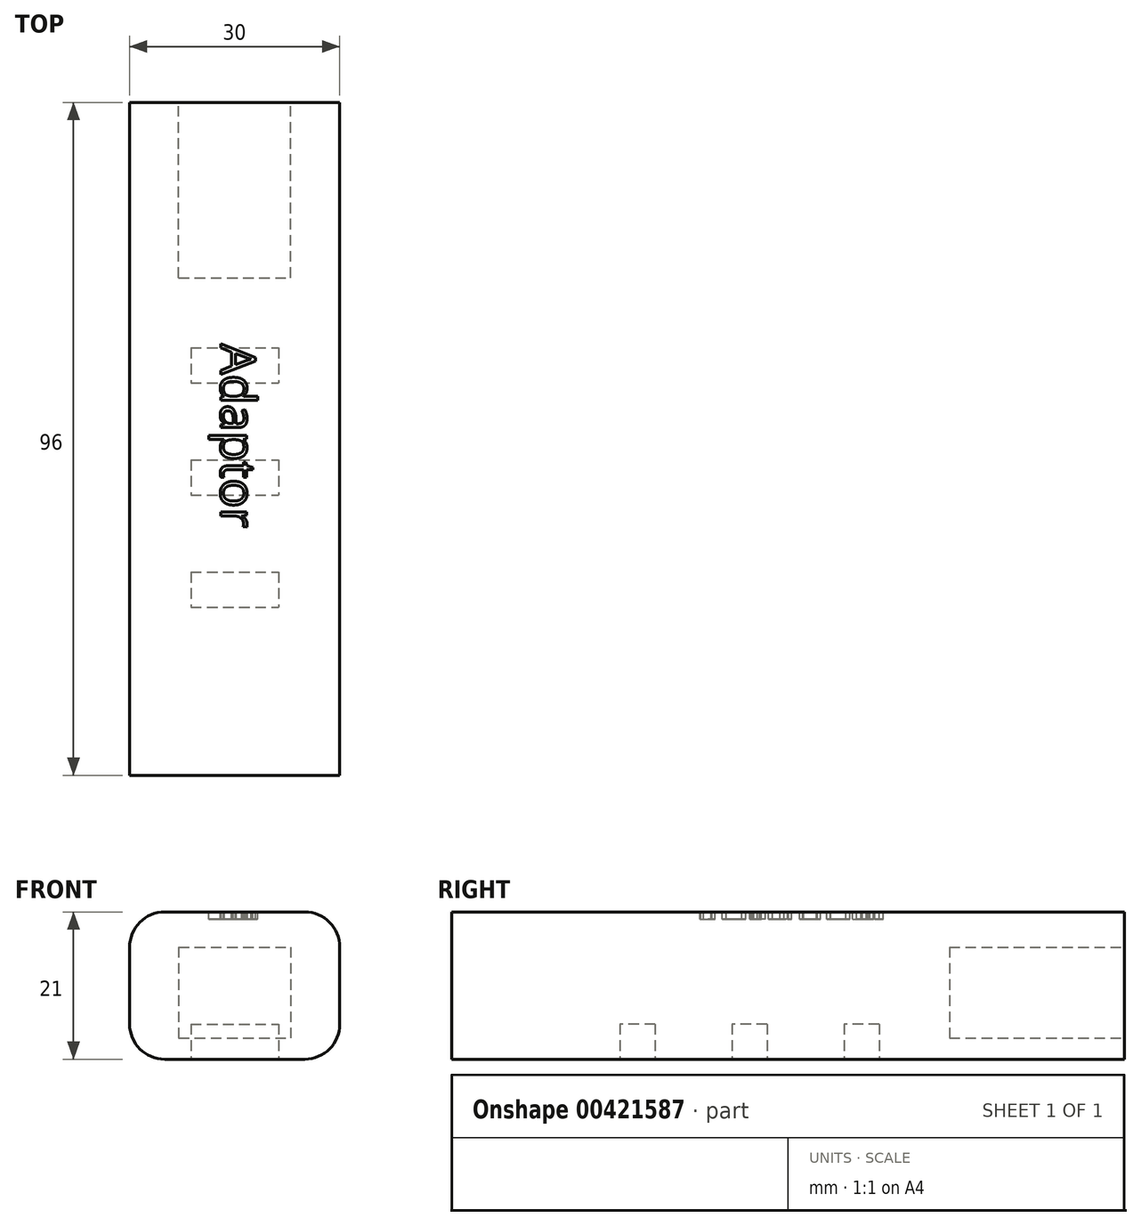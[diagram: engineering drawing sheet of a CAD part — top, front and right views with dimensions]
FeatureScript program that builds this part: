
annotation { "Feature Type Name" : "Feature", "Feature Type Description" : "" }
export const myFeature = defineFeature(function(context is Context, id is Id, definition is map)
    precondition{}
    {
        {
            var Q0;
            Q0=qCreatedBy(makeId("Top.planeOp"),FACE);
            var sketch = newSketch(context, id + "F0", { "sketchPlane" : qUnion([Q0])});
            skLineSegment(sketch, "E0.bottom", {"start": v(15, 48) * mm, "end": v(-15, 48) * mm});
            skLineSegment(sketch, "E0.top", {"start": v(15, -48) * mm, "end": v(-15, -48) * mm});
            skLineSegment(sketch, "E0.left", {"start": v(15, 48) * mm, "end": v(15, -48) * mm});
            skLineSegment(sketch, "E0.right", {"start": v(-15, 48) * mm, "end": v(-15, -48) * mm});
            skPoint(sketch, "E0.middle", {"position": v(0, 0) * mm});
            skSolve(sketch);
        }
        {
            var Q0;
            Q0 = qSketchRegion(id + "F0", true);
            extrude(context, id + "F1", {"entities" : qUnion([Q0]), "depth" : 21 * mm, "offsetDistance" : 25 * mm});
        }
        {
            var Q0;
            Q0=makeQuery(id+"F1.opExtrude","CAP_EDGE",EDGE,{"disambiguationData":[OSD([sQuery(id+"F0.wireOp",EDGE,"E0.left")])],"isStart":false});
            var Q1;
            Q1=makeQuery(id+"F1.opExtrude","CAP_EDGE",EDGE,{"disambiguationData":[OSD([sQuery(id+"F0.wireOp",EDGE,"E0.right")])],"isStart":false});
            var Q2;
            Q2=makeQuery(id+"F1.opExtrude","CAP_EDGE",EDGE,{"disambiguationData":[OSD([sQuery(id+"F0.wireOp",EDGE,"E0.left")])],"isStart":true});
            var Q3;
            Q3=makeQuery(id+"F1.opExtrude","CAP_EDGE",EDGE,{"disambiguationData":[OSD([sQuery(id+"F0.wireOp",EDGE,"E0.right")])],"isStart":true});
            fillet(context, id + "F2", {"entities" : qUnion([Q0, Q1, Q2, Q3]), "radius" : 5 * mm, "tangentPropagation" : true, "allowEdgeOverflow" : false});
        }
        {
            var Q0;
            Q0=makeQuery(id+"F1.opExtrude","SWEPT_FACE",FACE,{"disambiguationData":[OSD([sQuery(id+"F0.wireOp",EDGE,"E0.bottom")])]});
            var sketch = newSketch(context, id + "F3", { "sketchPlane" : qUnion([Q0])});
            skLineSegment(sketch, "E1.bottom", {"start": v(8, 16) * mm, "end": v(-8, 16) * mm});
            skLineSegment(sketch, "E1.top", {"start": v(8, 3) * mm, "end": v(-8, 3) * mm});
            skLineSegment(sketch, "E1.left", {"start": v(8, 16) * mm, "end": v(8, 3) * mm});
            skLineSegment(sketch, "E1.right", {"start": v(-8, 16) * mm, "end": v(-8, 3) * mm});
            skPoint(sketch, "E1.middle", {"position": v(0, 9.5) * mm});
            skSolve(sketch);
        }
        {
            var Q0;
            Q0=makeQuery(id+"F3.imprint","IMPRINT",FACE,{"disambiguationData":[TD([[makeQuery(id+"F3.imprint","IMPRINT",EDGE,{"derivedFrom":sQuery(id+"F3.wireOp",EDGE,"E1.bottom")}),1.0]])]});
            extrude(context, id + "F4", {"entities" : qUnion([Q0]), "operationType" : NewBodyOperationType.REMOVE, "oppositeDirection" : true, "depth" : 25 * mm, "offsetDistance" : 25 * mm});
        }
        {
            var Q0;
            Q0=makeQuery(id+"F1.opExtrude","CAP_FACE",FACE,{"disambiguationData":[OSD([sQuery(id+"F0.wireOp",EDGE,"E0.bottom"),sQuery(id+"F0.wireOp",EDGE,"E0.top"),sQuery(id+"F0.wireOp",EDGE,"E0.left"),sQuery(id+"F0.wireOp",EDGE,"E0.right")])],"isStart":false});
            cPlane(context, id + "F5", {"entities" : qUnion([Q0]), "cplaneType" : CPlaneType.OFFSET, "offset" : 0 * mm, "width" : 150 * mm, "height" : 150 * mm});
        }
        {
            var Q0;
            Q0=qCreatedBy(id+"F5.planeOp",FACE);
            var sketch = newSketch(context, id + "F6", { "sketchPlane" : qUnion([Q0])});
            skText(sketch, "E2", { "text": "Adaptor\n", "fontName": "OpenSans-Regular.ttf"});
            const initialGuessF6  = {"E2": [-0.00201, 0.01358, 0, -1, 0.005]};
            skSetInitialGuess(sketch, initialGuessF6);
            skSolve(sketch);
        }
        {
            var Q0;
            Q0 = qSketchRegion(id + "F6", true);
            extrude(context, id + "F7", {"entities" : qUnion([Q0]), "operationType" : NewBodyOperationType.REMOVE, "oppositeDirection" : true, "depth" : 1 * mm, "offsetDistance" : 25 * mm});
        }
        {
            var Q0;
            Q0=makeQuery(id+"F1.opExtrude","CAP_FACE",FACE,{"disambiguationData":[OSD([sQuery(id+"F0.wireOp",EDGE,"E0.bottom"),sQuery(id+"F0.wireOp",EDGE,"E0.top"),sQuery(id+"F0.wireOp",EDGE,"E0.left"),sQuery(id+"F0.wireOp",EDGE,"E0.right")])],"isStart":true});
            cPlane(context, id + "F8", {"entities" : qUnion([Q0]), "cplaneType" : CPlaneType.OFFSET, "offset" : 0 * mm, "width" : 150 * mm, "height" : 150 * mm});
        }
        {
            var Q0;
            Q0=qCreatedBy(id+"F8.planeOp",FACE);
            var sketch = newSketch(context, id + "F9", { "sketchPlane" : qUnion([Q0])});
            skLineSegment(sketch, "E3.bottom", {"start": v(-6.25, -13) * mm, "end": v(6.25, -13) * mm});
            skLineSegment(sketch, "E3.top", {"start": v(-6.25, -8) * mm, "end": v(6.25, -8) * mm});
            skLineSegment(sketch, "E3.left", {"start": v(-6.25, -13) * mm, "end": v(-6.25, -8) * mm});
            skLineSegment(sketch, "E3.right", {"start": v(6.25, -13) * mm, "end": v(6.25, -8) * mm});
            skPoint(sketch, "E3.middle", {"position": v(0, -10.5) * mm});
            skLineSegment(sketch, "E4.bottom", {"start": v(-6.25, 3) * mm, "end": v(6.25, 3) * mm});
            skLineSegment(sketch, "E4.top", {"start": v(-6.25, 8) * mm, "end": v(6.25, 8) * mm});
            skLineSegment(sketch, "E4.left", {"start": v(-6.25, 3) * mm, "end": v(-6.25, 8) * mm});
            skLineSegment(sketch, "E4.right", {"start": v(6.25, 3) * mm, "end": v(6.25, 8) * mm});
            skPoint(sketch, "E4.middle", {"position": v(0, 5.5) * mm});
            skLineSegment(sketch, "E5.bottom", {"start": v(-6.25, 19) * mm, "end": v(6.25, 19) * mm});
            skLineSegment(sketch, "E5.top", {"start": v(-6.25, 24) * mm, "end": v(6.25, 24) * mm});
            skLineSegment(sketch, "E5.left", {"start": v(-6.25, 19) * mm, "end": v(-6.25, 24) * mm});
            skLineSegment(sketch, "E5.right", {"start": v(6.25, 19) * mm, "end": v(6.25, 24) * mm});
            skPoint(sketch, "E5.middle", {"position": v(0, 21.5) * mm});
            skSolve(sketch);
        }
        {
            var Q0;
            Q0=makeQuery(id+"F9.imprint","IMPRINT",FACE,{"disambiguationData":[TD([[makeQuery(id+"F9.imprint","IMPRINT",EDGE,{"derivedFrom":sQuery(id+"F9.wireOp",EDGE,"E5.bottom")}),1.0]])]});
            var Q1;
            Q1=makeQuery(id+"F9.imprint","IMPRINT",FACE,{"disambiguationData":[TD([[makeQuery(id+"F9.imprint","IMPRINT",EDGE,{"derivedFrom":sQuery(id+"F9.wireOp",EDGE,"E4.bottom")}),1.0]])]});
            var Q2;
            Q2=makeQuery(id+"F9.imprint","IMPRINT",FACE,{"disambiguationData":[TD([[makeQuery(id+"F9.imprint","IMPRINT",EDGE,{"derivedFrom":sQuery(id+"F9.wireOp",EDGE,"E3.bottom")}),1.0]])]});
            extrude(context, id + "F10", {"entities" : qUnion([Q0, Q1, Q2]), "operationType" : NewBodyOperationType.REMOVE, "oppositeDirection" : true, "depth" : 5 * mm, "offsetDistance" : 25 * mm});
        }
    });
